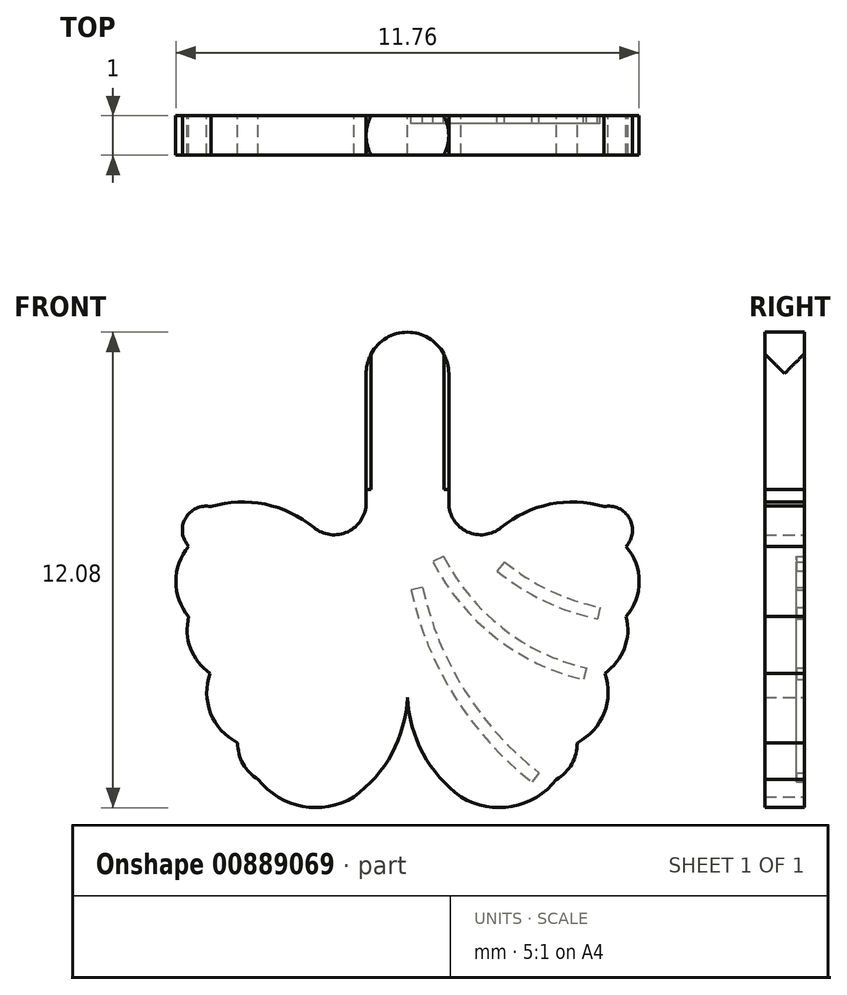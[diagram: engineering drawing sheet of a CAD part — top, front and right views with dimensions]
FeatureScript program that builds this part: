
annotation { "Feature Type Name" : "Feature", "Feature Type Description" : "" }
export const myFeature = defineFeature(function(context is Context, id is Id, definition is map)
    precondition{}
    {
        {
            var Q0;
            Q0=qCreatedBy(makeId("Front.planeOp"),FACE);
            var sketch = newSketch(context, id + "F0", { "sketchPlane" : qUnion([Q0])});
            skLineSegment(sketch, "E0", {"start": v(0, 4.31) * mm, "end": v(0, 0) * mm, "construction": true});
            skLineSegment(sketch, "E1", {"start": v(6, 0) * mm, "end": v(0, 0) * mm, "construction": true});
            skLineSegment(sketch, "E2", {"start": v(1.05, 6.95) * mm, "end": v(1.05, 3.67) * mm});
            skArc(sketch, "E3", {"start": v(0, -1.28) * mm, "mid": v(0.4, -2.7) * mm, "end": v(1.36, -3.8) * mm});
            skArc(sketch, "E4", {"start": v(1.36, -3.8) * mm, "mid": v(2.66, -4.05) * mm, "end": v(3.79, -3.36) * mm});
            skArc(sketch, "E5", {"start": v(3.79, -3.36) * mm, "mid": v(4.18, -2.97) * mm, "end": v(4.31, -2.43) * mm});
            skArc(sketch, "E6", {"start": v(4.31, -2.43) * mm, "mid": v(5, -1.68) * mm, "end": v(5.01, -0.66) * mm});
            skArc(sketch, "E7", {"start": v(5.01, -0.66) * mm, "mid": v(5.51, -0.03) * mm, "end": v(5.56, 0.77) * mm});
            skArc(sketch, "E8", {"start": v(5.56, 0.77) * mm, "mid": v(5.88, 1.67) * mm, "end": v(5.56, 2.56) * mm});
            skArc(sketch, "E9", {"start": v(1.05, 3.67) * mm, "mid": v(1.52, 2.93) * mm, "end": v(2.38, 3.04) * mm});
            skArc(sketch, "E10", {"start": v(5.56, 2.56) * mm, "mid": v(5.64, 3.27) * mm, "end": v(5, 3.57) * mm});
            skArc(sketch, "E11", {"start": v(5, 3.57) * mm, "mid": v(3.62, 3.63) * mm, "end": v(2.38, 3.04) * mm});
            skLineSegment(sketch, "E12.left", {"start": v(1.05, 6.95) * mm, "end": v(1.05, 6.95) * mm});
            skLineSegment(sketch, "E12.right", {"start": v(0, 6.95) * mm, "end": v(0, 6.95) * mm});
            skLineSegment(sketch, "E13.bottom", {"start": v(0, -1.28) * mm, "end": v(0, -1.28) * mm});
            skLineSegment(sketch, "E13.left", {"start": v(0, -1.28) * mm, "end": v(0, 8) * mm});
            skLineSegment(sketch, "E13.right", {"start": v(0, -1.28) * mm, "end": v(0, 6.95) * mm});
            skArc(sketch, "E14", {"start": v(1.05, 6.95) * mm, "mid": v(0.74, 7.7) * mm, "end": v(0, 8) * mm});
            skSolve(sketch);
        }
        {
            var Q0;
            Q0=makeQuery(id+"F0.imprint","IMPRINT",FACE,{"disambiguationData":[TD([[makeQuery(id+"F0.imprint","IMPRINT",EDGE,{"derivedFrom":sQuery(id+"F0.wireOp",EDGE,"E2")}),-1.0]])]});
            extrude(context, id + "F1", {"entities" : qUnion([Q0]), "depth" : .5 * mm, "offsetDistance" : 25 * mm, "hasSecondDirection" : true, "secondDirectionOppositeDirection" : true, "secondDirectionDepth" : .5 * mm});
        }
        {
            var Q0;
            Q0=makeQuery(id+"F1.opExtrude","SWEPT_BODY",BODY,{"disambiguationData":[OSD([sQuery(id+"F0.wireOp",EDGE,"E2"),sQuery(id+"F0.wireOp",EDGE,"E3"),sQuery(id+"F0.wireOp",EDGE,"E4"),sQuery(id+"F0.wireOp",EDGE,"E5"),sQuery(id+"F0.wireOp",EDGE,"E6"),sQuery(id+"F0.wireOp",EDGE,"E7"),sQuery(id+"F0.wireOp",EDGE,"E8"),sQuery(id+"F0.wireOp",EDGE,"E9"),sQuery(id+"F0.wireOp",EDGE,"E10"),sQuery(id+"F0.wireOp",EDGE,"E11"),sQuery(id+"F0.wireOp",EDGE,"E13.left"),sQuery(id+"F0.wireOp",EDGE,"E13.right"),sQuery(id+"F0.wireOp",EDGE,"E14")])]});
            var Q1;
            Q1=makeQuery(id+"F1.opExtrude","SWEPT_FACE",FACE,{"disambiguationData":[OSD([sQuery(id+"F0.wireOp",EDGE,"E13.left"),sQuery(id+"F0.wireOp",EDGE,"E13.right")])]});
            mirror(context, id + "F2", {"operationType" : NewBodyOperationType.ADD, "entities" : qUnion([Q0]), "mirrorPlane" : qUnion([Q1])});
        }
        {
            var Q0;
            Q0=qCreatedBy(makeId("Top.planeOp"),FACE);
            cPlane(context, id + "F3", {"entities" : qUnion([Q0]), "cplaneType" : CPlaneType.OFFSET, "offset" : 10 * mm, "width" : 150 * mm, "height" : 150 * mm});
        }
        {
            var Q0;
            Q0=qCreatedBy(id+"F3.planeOp",FACE);
            var sketch = newSketch(context, id + "F4", { "sketchPlane" : qUnion([Q0])});
            skCircle(sketch, "E15", {"center": v(0, 0) * mm, "radius": 1.05 * mm});
            skCircle(sketch, "E16", {"center": v(0, 0) * mm, "radius": 3 * mm});
            skSolve(sketch);
        }
        {
            var Q0;
            Q0=makeQuery(id+"F4.imprint","IMPRINT",FACE,{"disambiguationData":[TD([[makeQuery(id+"F4.imprint","IMPRINT",EDGE,{"derivedFrom":sQuery(id+"F4.wireOp",EDGE,"E15")}),-1.0]])]});
            extrude(context, id + "F5", {"entities" : qUnion([Q0]), "operationType" : NewBodyOperationType.REMOVE, "oppositeDirection" : true, "depth" : 6 * mm, "offsetDistance" : 25 * mm});
        }
        {
            var Q0;
            {var subQ0=makeQuery(id+"F1.opExtrude","CAP_FACE",FACE,{"disambiguationData":[OSD([sQuery(id+"F0.wireOp",EDGE,"E2"),sQuery(id+"F0.wireOp",EDGE,"E3"),sQuery(id+"F0.wireOp",EDGE,"E4"),sQuery(id+"F0.wireOp",EDGE,"E5"),sQuery(id+"F0.wireOp",EDGE,"E6"),sQuery(id+"F0.wireOp",EDGE,"E7"),sQuery(id+"F0.wireOp",EDGE,"E8"),sQuery(id+"F0.wireOp",EDGE,"E9"),sQuery(id+"F0.wireOp",EDGE,"E10"),sQuery(id+"F0.wireOp",EDGE,"E11"),sQuery(id+"F0.wireOp",EDGE,"E13.left"),sQuery(id+"F0.wireOp",EDGE,"E13.right"),sQuery(id+"F0.wireOp",EDGE,"E14")])],"isStart":true});Q0=makeQuery(id+"F2.boolean.opBoolean","MERGE",FACE,{"derivedFrom":[subQ0,makeQuery(id+"F2.opPattern","COPY",FACE,{"derivedFrom":subQ0,"instanceName":"1"})]});}
            var sketch = newSketch(context, id + "F6", { "sketchPlane" : qUnion([Q0])});
            skArc(sketch, "E17", {"start": v(-3.34, -3.19) * mm, "mid": v(-1.45, -1.1) * mm, "end": v(-0.39, 1.52) * mm});
            skArc(sketch, "E18", {"start": v(-4.54, -0.53) * mm, "mid": v(-2.42, 0.48) * mm, "end": v(-0.92, 2.3) * mm});
            skArc(sketch, "E19", {"start": v(-4.9, 1.01) * mm, "mid": v(-3.6, 1.44) * mm, "end": v(-2.47, 2.17) * mm});
            skArc(sketch, "E20.0", {"start": v(-4.83, 0.72) * mm, "mid": v(-3.48, 1.17) * mm, "end": v(-2.28, 1.94) * mm});
            skArc(sketch, "E21.0", {"start": v(-4.48, -0.83) * mm, "mid": v(-2.23, 0.25) * mm, "end": v(-0.65, 2.17) * mm});
            skArc(sketch, "E22.0", {"start": v(-3.16, -3.43) * mm, "mid": v(-1.2, -1.25) * mm, "end": v(-0.1, 1.46) * mm});
            skLineSegment(sketch, "E23", {"start": v(-4.9, 1.01) * mm, "end": v(-4.83, 0.72) * mm});
            skLineSegment(sketch, "E24", {"start": v(-4.54, -0.53) * mm, "end": v(-4.48, -0.83) * mm});
            skLineSegment(sketch, "E25", {"start": v(-3.34, -3.19) * mm, "end": v(-3.16, -3.43) * mm});
            skLineSegment(sketch, "E26", {"start": v(-2.47, 2.17) * mm, "end": v(-2.28, 1.94) * mm});
            skLineSegment(sketch, "E27", {"start": v(-0.92, 2.3) * mm, "end": v(-0.65, 2.17) * mm});
            skLineSegment(sketch, "E28", {"start": v(-0.39, 1.52) * mm, "end": v(-0.1, 1.46) * mm});
            skSolve(sketch);
        }
        {
            var Q0;
            Q0=makeQuery(id+"F6.imprint","IMPRINT",FACE,{"disambiguationData":[TD([[makeQuery(id+"F6.imprint","IMPRINT",EDGE,{"derivedFrom":sQuery(id+"F6.wireOp",EDGE,"E19")}),-1.0]])]});
            var Q1;
            Q1=makeQuery(id+"F6.imprint","IMPRINT",FACE,{"disambiguationData":[TD([[makeQuery(id+"F6.imprint","IMPRINT",EDGE,{"derivedFrom":sQuery(id+"F6.wireOp",EDGE,"E18")}),-1.0]])]});
            var Q2;
            Q2=makeQuery(id+"F6.imprint","IMPRINT",FACE,{"disambiguationData":[TD([[makeQuery(id+"F6.imprint","IMPRINT",EDGE,{"derivedFrom":sQuery(id+"F6.wireOp",EDGE,"E17")}),-1.0]])]});
            extrude(context, id + "F7", {"entities" : qUnion([Q0, Q1, Q2]), "operationType" : NewBodyOperationType.REMOVE, "oppositeDirection" : true, "depth" : .2 * mm, "offsetDistance" : 25 * mm});
        }
    });
